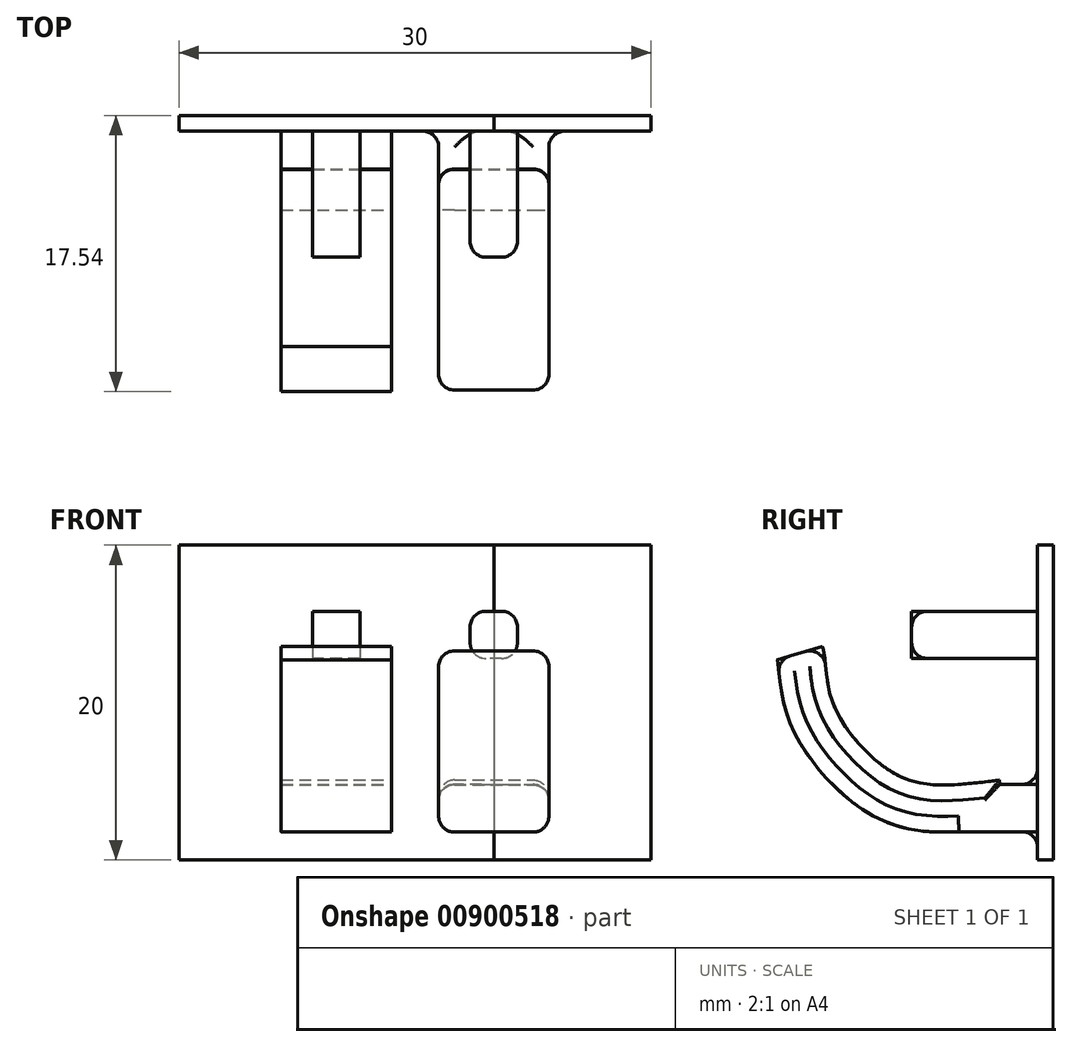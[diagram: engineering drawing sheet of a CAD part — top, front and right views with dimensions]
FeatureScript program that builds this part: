
annotation { "Feature Type Name" : "Feature", "Feature Type Description" : "" }
export const myFeature = defineFeature(function(context is Context, id is Id, definition is map)
    precondition{}
    {
        {
            var Q0;
            Q0=qCreatedBy(makeId("Front.planeOp"),FACE);
            var sketch = newSketch(context, id + "F0", { "sketchPlane" : qUnion([Q0])});
            skLineSegment(sketch, "E0.bottom", {"start": v(17.5, 10) * mm, "end": v(-17.5, 10) * mm});
            skLineSegment(sketch, "E0.top", {"start": v(17.5, -10) * mm, "end": v(-17.5, -10) * mm});
            skLineSegment(sketch, "E0.left", {"start": v(17.5, 10) * mm, "end": v(17.5, -10) * mm});
            skLineSegment(sketch, "E0.right", {"start": v(-17.5, 10) * mm, "end": v(-17.5, -10) * mm});
            skPoint(sketch, "E0.middle", {"position": v(0, 0) * mm});
            skSolve(sketch);
        }
        {
            var Q0;
            Q0=makeQuery(id+"F0.imprint","IMPRINT",FACE,{"disambiguationData":[TD([[makeQuery(id+"F0.imprint","IMPRINT",EDGE,{"derivedFrom":sQuery(id+"F0.wireOp",EDGE,"E0.bottom")}),1.0]])]});
            extrude(context, id + "F1", {"entities" : qUnion([Q0]), "oppositeDirection" : true, "depth" : 1 * mm, "offsetDistance" : 25 * mm});
        }
        {
            var Q0;
            Q0=makeQuery(id+"F1.opExtrude","CAP_FACE",FACE,{"disambiguationData":[OSD([sQuery(id+"F0.wireOp",EDGE,"E0.bottom"),sQuery(id+"F0.wireOp",EDGE,"E0.top"),sQuery(id+"F0.wireOp",EDGE,"E0.left"),sQuery(id+"F0.wireOp",EDGE,"E0.right")])],"isStart":true});
            var sketch = newSketch(context, id + "F2", { "sketchPlane" : qUnion([Q0])});
            skLineSegment(sketch, "E1.bottom", {"start": v(9, 5.8) * mm, "end": v(6, 5.8) * mm});
            skLineSegment(sketch, "E1.top", {"start": v(9, 2.8) * mm, "end": v(6, 2.8) * mm});
            skLineSegment(sketch, "E1.left", {"start": v(9, 5.8) * mm, "end": v(9, 2.8) * mm});
            skLineSegment(sketch, "E1.right", {"start": v(6, 5.8) * mm, "end": v(6, 2.8) * mm});
            skLineSegment(sketch, "E2.bottom", {"start": v(4, -5.2) * mm, "end": v(11, -5.2) * mm});
            skLineSegment(sketch, "E2.top", {"start": v(4, -8.2) * mm, "end": v(11, -8.2) * mm});
            skLineSegment(sketch, "E2.left", {"start": v(4, -5.2) * mm, "end": v(4, -8.2) * mm});
            skLineSegment(sketch, "E2.right", {"start": v(11, -5.2) * mm, "end": v(11, -8.2) * mm});
            skPoint(sketch, "E3", {"position": v(9, -5.2) * mm});
            skSolve(sketch);
        }
        {
            var Q0;
            Q0=makeQuery(id+"F2.imprint","IMPRINT",FACE,{"disambiguationData":[TD([[makeQuery(id+"F2.imprint","IMPRINT",EDGE,{"derivedFrom":sQuery(id+"F2.wireOp",EDGE,"E1.bottom")}),1.0]])]});
            extrude(context, id + "F3", {"entities" : qUnion([Q0]), "operationType" : NewBodyOperationType.ADD, "depth" : 8 * mm, "offsetDistance" : 25 * mm});
        }
        {
            var Q0;
            Q0=makeQuery(id+"F2.imprint","IMPRINT",FACE,{"disambiguationData":[TD([[makeQuery(id+"F2.imprint","IMPRINT",EDGE,{"derivedFrom":sQuery(id+"F2.wireOp",EDGE,"E2.bottom")}),-1.0]])]});
            extrude(context, id + "F4", {"entities" : qUnion([Q0]), "operationType" : NewBodyOperationType.ADD, "depth" : 5 * mm, "offsetDistance" : 25 * mm});
        }
        {
            var Q0;
            Q0=qCreatedBy(makeId("Right.planeOp"),FACE);
            var sketch = newSketch(context, id + "F5", { "sketchPlane" : qUnion([Q0])});
            skFitSpline(sketch, "E4", {"points": [v(-2.3, -6.7) * mm, v(-8.47, -6.7) * mm, v(-12.67, -3.8) * mm, v(-14.88, 0) * mm, v(-15.3, 2.78) * mm, v(-15.37, 3.06) * mm], "startDerivative": vector(-23.63, -2.94) * mm, "endDerivative": vector(-1.22, 3.43) * mm});
            skSolve(sketch);
        }
        {
            var Q0;
            Q0=makeQuery(id+"F4.opExtrude","CAP_FACE",FACE,{"disambiguationData":[OSD([sQuery(id+"F2.wireOp",EDGE,"E2.bottom"),sQuery(id+"F2.wireOp",EDGE,"E2.top"),sQuery(id+"F2.wireOp",EDGE,"E2.left"),sQuery(id+"F2.wireOp",EDGE,"E2.right")])],"isStart":false});
            var Q1;
            Q1=sQuery(id+"F5.wireOp",EDGE,"E4");
            sweep(context, id + "F6", {"operationType" : NewBodyOperationType.ADD, "profiles" : qUnion([Q0]), "path" : qUnion([Q1])});
        }
        {
            var Q0;
            Q0=makeQuery(id+"F1.opExtrude","SWEPT_BODY",BODY,{"disambiguationData":[OSD([sQuery(id+"F0.wireOp",EDGE,"E0.bottom"),sQuery(id+"F0.wireOp",EDGE,"E0.top"),sQuery(id+"F0.wireOp",EDGE,"E0.left"),sQuery(id+"F0.wireOp",EDGE,"E0.right")])]});
            transform(context, id + "F7", {"entities" : qUnion([Q0]), "transformType" : TransformType.TRANSLATION_3D, "dx" : 10 * mm, "dy" : 0 * mm, "dz" : 0 * mm, "makeCopy" : true});
        }
        {
            var Q0;
            Q0=makeQuery(id+"F3.opExtrude","CAP_FACE",FACE,{"disambiguationData":[OSD([sQuery(id+"F2.wireOp",EDGE,"E1.bottom"),sQuery(id+"F2.wireOp",EDGE,"E1.top"),sQuery(id+"F2.wireOp",EDGE,"E1.left"),sQuery(id+"F2.wireOp",EDGE,"E1.right")])],"isStart":false});
            var Q1;
            Q1=makeQuery(id+"F7.opPattern","COPY",FACE,{"derivedFrom":makeQuery(id+"F3.opExtrude","CAP_FACE",FACE,{"disambiguationData":[OSD([sQuery(id+"F2.wireOp",EDGE,"E1.bottom"),sQuery(id+"F2.wireOp",EDGE,"E1.top"),sQuery(id+"F2.wireOp",EDGE,"E1.left"),sQuery(id+"F2.wireOp",EDGE,"E1.right")])],"isStart":false}),"instanceName":"1"});
            var Q2;
            Q2=makeQuery(id+"F7.opPattern","COPY",FACE,{"derivedFrom":makeQuery(id+"F6.opSweep","CAP_FACE",FACE,{"disambiguationData":[OSD([sQuery(id+"F2.wireOp",EDGE,"E2.bottom"),sQuery(id+"F2.wireOp",EDGE,"E2.top"),sQuery(id+"F2.wireOp",EDGE,"E2.left"),sQuery(id+"F2.wireOp",EDGE,"E2.right"),sQuery(id+"F5.wireOp",VERTEX,"E4.end")])],"isStart":false}),"instanceName":"1"});
            var Q3;
            Q3=makeQuery(id+"F6.opSweep","CAP_FACE",FACE,{"disambiguationData":[OSD([sQuery(id+"F2.wireOp",EDGE,"E2.bottom"),sQuery(id+"F2.wireOp",EDGE,"E2.top"),sQuery(id+"F2.wireOp",EDGE,"E2.left"),sQuery(id+"F2.wireOp",EDGE,"E2.right"),sQuery(id+"F5.wireOp",VERTEX,"E4.end")])],"isStart":false});
            var Q4;
            {var subQ0=sQuery(id+"F2.wireOp",EDGE,"E2.right");Q4=makeQuery(id+"F7.opPattern","COPY",FACE,{"derivedFrom":makeQuery(id+"F6.boolean.opBoolean","MERGE",FACE,{"derivedFrom":[makeQuery(id+"F4.opExtrude","SWEPT_FACE",FACE,{"disambiguationData":[OSD([subQ0])]}),makeQuery(id+"F6.opSweep","SWEPT_FACE",FACE,{"disambiguationData":[OSD([subQ0,sQuery(id+"F5.wireOp",EDGE,"E4")])]})]}),"instanceName":"1"});}
            var Q5;
            {var subQ0=sQuery(id+"F2.wireOp",EDGE,"E2.left");Q5=makeQuery(id+"F6.boolean.opBoolean","MERGE",FACE,{"derivedFrom":[makeQuery(id+"F4.opExtrude","SWEPT_FACE",FACE,{"disambiguationData":[OSD([subQ0])]}),makeQuery(id+"F6.opSweep","SWEPT_FACE",FACE,{"disambiguationData":[OSD([subQ0,sQuery(id+"F5.wireOp",EDGE,"E4")])]})]});}
            var Q6;
            Q6=makeQuery(id+"F3.opExtrude","SWEPT_FACE",FACE,{"disambiguationData":[OSD([sQuery(id+"F2.wireOp",EDGE,"E1.bottom")])]});
            var Q7;
            Q7=makeQuery(id+"F7.opPattern","COPY",EDGE,{"derivedFrom":makeQuery(id+"F3.opExtrude","SWEPT_EDGE",EDGE,{"disambiguationData":[OSD([sQuery(id+"F2.wireOp",EDGE,"E1.top"),sQuery(id+"F2.wireOp",EDGE,"E1.left")])]}),"instanceName":"1"});
            var Q8;
            Q8=makeQuery(id+"F7.opPattern","COPY",EDGE,{"derivedFrom":makeQuery(id+"F3.opExtrude","SWEPT_EDGE",EDGE,{"disambiguationData":[OSD([sQuery(id+"F2.wireOp",EDGE,"E1.top"),sQuery(id+"F2.wireOp",EDGE,"E1.right")])]}),"instanceName":"1"});
            var Q9;
            Q9=makeQuery(id+"F7.opPattern","COPY",EDGE,{"derivedFrom":makeQuery(id+"F3.opExtrude","SWEPT_EDGE",EDGE,{"disambiguationData":[OSD([sQuery(id+"F2.wireOp",EDGE,"E1.bottom"),sQuery(id+"F2.wireOp",EDGE,"E1.left")])]}),"instanceName":"1"});
            var Q10;
            Q10=makeQuery(id+"F7.opPattern","COPY",EDGE,{"derivedFrom":makeQuery(id+"F3.opExtrude","SWEPT_EDGE",EDGE,{"disambiguationData":[OSD([sQuery(id+"F2.wireOp",EDGE,"E1.bottom"),sQuery(id+"F2.wireOp",EDGE,"E1.right")])]}),"instanceName":"1"});
            var Q11;
            {var subQ0=sQuery(id+"F2.wireOp",EDGE,"E2.left");Q11=makeQuery(id+"F7.opPattern","COPY",FACE,{"derivedFrom":makeQuery(id+"F6.boolean.opBoolean","MERGE",FACE,{"derivedFrom":[makeQuery(id+"F4.opExtrude","SWEPT_FACE",FACE,{"disambiguationData":[OSD([subQ0])]}),makeQuery(id+"F6.opSweep","SWEPT_FACE",FACE,{"disambiguationData":[OSD([subQ0,sQuery(id+"F5.wireOp",EDGE,"E4")])]})]}),"instanceName":"1"});}
            var Q12;
            {var subQ0=sQuery(id+"F2.wireOp",EDGE,"E2.right");Q12=makeQuery(id+"F6.boolean.opBoolean","MERGE",FACE,{"derivedFrom":[makeQuery(id+"F4.opExtrude","SWEPT_FACE",FACE,{"disambiguationData":[OSD([subQ0])]}),makeQuery(id+"F6.opSweep","SWEPT_FACE",FACE,{"disambiguationData":[OSD([subQ0,sQuery(id+"F5.wireOp",EDGE,"E4")])]})]});}
            var Q13;
            Q13=makeQuery(id+"F3.opExtrude","SWEPT_EDGE",EDGE,{"disambiguationData":[OSD([sQuery(id+"F2.wireOp",EDGE,"E1.top"),sQuery(id+"F2.wireOp",EDGE,"E1.right")])]});
            var Q14;
            Q14=makeQuery(id+"F3.opExtrude","SWEPT_EDGE",EDGE,{"disambiguationData":[OSD([sQuery(id+"F2.wireOp",EDGE,"E1.top"),sQuery(id+"F2.wireOp",EDGE,"E1.left")])]});
            var Q15;
            Q15=makeQuery(id+"F7.opPattern","COPY",EDGE,{"derivedFrom":makeQuery(id+"F3.opExtrude","CAP_EDGE",EDGE,{"disambiguationData":[OSD([sQuery(id+"F2.wireOp",EDGE,"E1.bottom")])],"isStart":true}),"instanceName":"1"});
            fillet(context, id + "F8", {"entities" : qUnion([Q0, Q1, Q2, Q3, Q4, Q5, Q6, Q7, Q8, Q9, Q10, Q11, Q12, Q13, Q14, Q15]), "radius" : 1 * mm, "tangentPropagation" : true, "allowEdgeOverflow" : false});
        }
        {
            var Q0;
            Q0=makeQuery(id+"F1.opExtrude","SWEPT_FACE",FACE,{"disambiguationData":[OSD([sQuery(id+"F0.wireOp",EDGE,"E0.right")])]});
            extrude(context, id + "F9", {"entities" : qUnion([Q0]), "operationType" : NewBodyOperationType.REMOVE, "oppositeDirection" : true, "depth" : 15 * mm, "offsetDistance" : 25 * mm});
        }
    });
